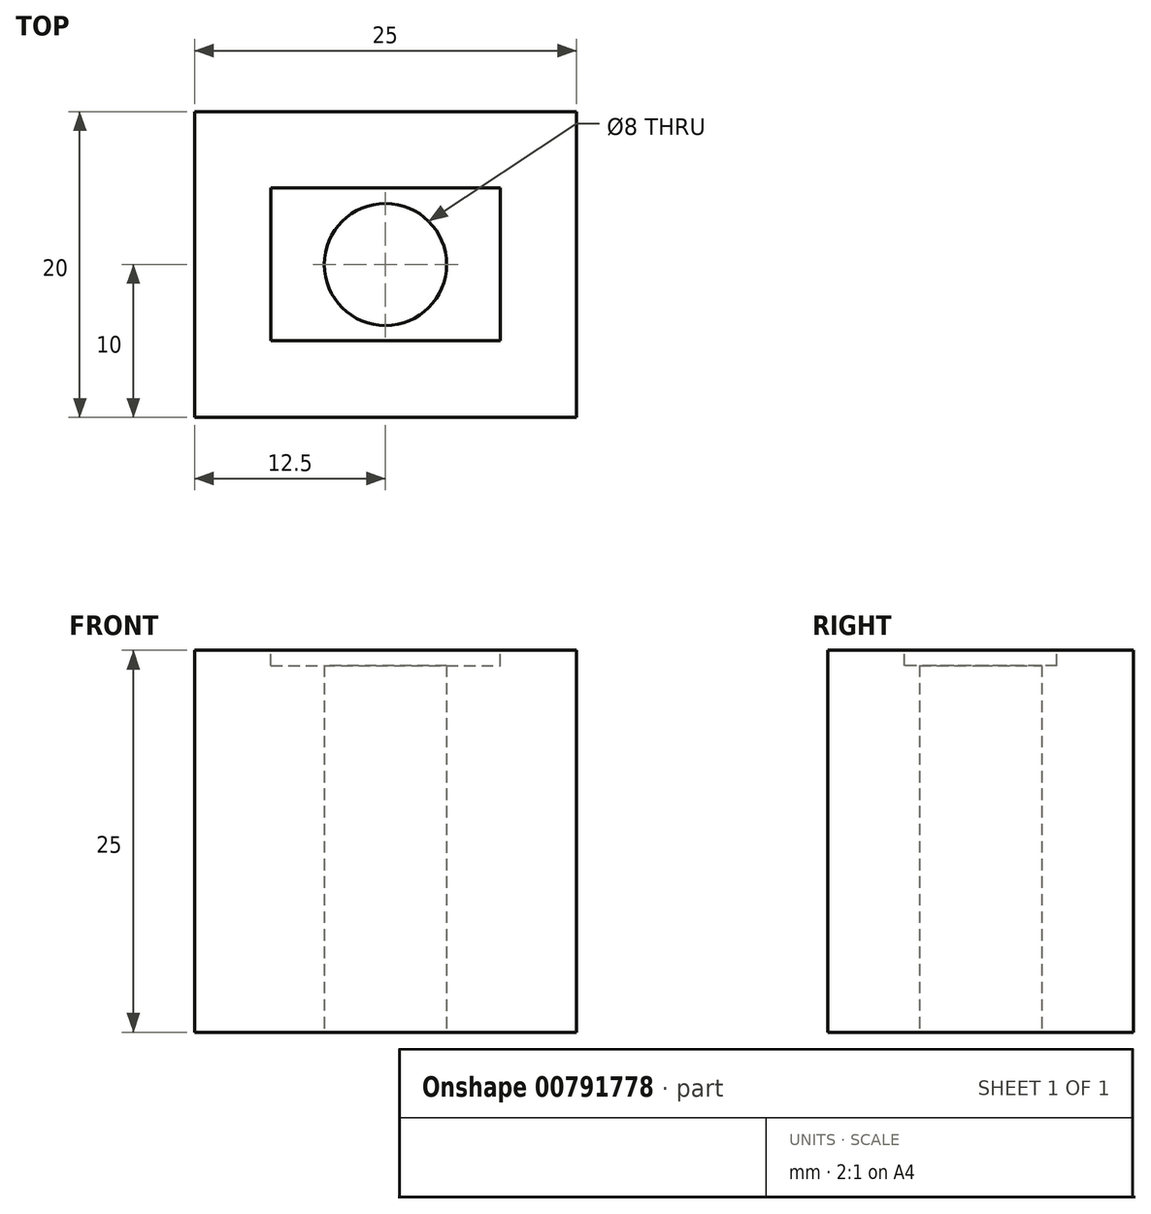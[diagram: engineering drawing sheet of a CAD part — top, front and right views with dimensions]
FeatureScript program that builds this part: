
annotation { "Feature Type Name" : "Feature", "Feature Type Description" : "" }
export const myFeature = defineFeature(function(context is Context, id is Id, definition is map)
    precondition{}
    {
        {
            var Q0;
            Q0=qCreatedBy(makeId("Top.planeOp"),FACE);
            var sketch = newSketch(context, id + "F0", { "sketchPlane" : qUnion([Q0])});
            skLineSegment(sketch, "E0.bottom", {"start": v(-12.5, 10) * mm, "end": v(12.5, 10) * mm});
            skLineSegment(sketch, "E0.top", {"start": v(-12.5, -10) * mm, "end": v(12.5, -10) * mm});
            skLineSegment(sketch, "E0.left", {"start": v(-12.5, 10) * mm, "end": v(-12.5, -10) * mm});
            skLineSegment(sketch, "E0.right", {"start": v(12.5, 10) * mm, "end": v(12.5, -10) * mm});
            skCircle(sketch, "E1", {"center": v(0, 0) * mm, "radius": 4 * mm});
            skSolve(sketch);
        }
        {
            var Q0;
            Q0 = qSketchRegion(id + "F0", true);
            extrude(context, id + "F1", {"entities" : qUnion([Q0]), "depth" : 25 * mm, "offsetDistance" : 25 * mm});
        }
        {
            var Q0;
            Q0=makeQuery(id+"F1.opExtrude","CAP_FACE",FACE,{"disambiguationData":[OSD([sQuery(id+"F0.wireOp",EDGE,"E0.bottom"),sQuery(id+"F0.wireOp",EDGE,"E0.top"),sQuery(id+"F0.wireOp",EDGE,"E0.left"),sQuery(id+"F0.wireOp",EDGE,"E0.right"),sQuery(id+"F0.wireOp",EDGE,"E1")])],"isStart":false});
            var sketch = newSketch(context, id + "F2", { "sketchPlane" : qUnion([Q0])});
            skLineSegment(sketch, "E2.bottom", {"start": v(-7.5, 5) * mm, "end": v(7.5, 5) * mm});
            skLineSegment(sketch, "E2.top", {"start": v(-7.5, -5) * mm, "end": v(7.5, -5) * mm});
            skLineSegment(sketch, "E2.left", {"start": v(-7.5, 5) * mm, "end": v(-7.5, -5) * mm});
            skLineSegment(sketch, "E2.right", {"start": v(7.5, 5) * mm, "end": v(7.5, -5) * mm});
            skSolve(sketch);
        }
        {
            var Q0;
            Q0 = qSketchRegion(id + "F2", true);
            extrude(context, id + "F3", {"entities" : qUnion([Q0]), "operationType" : NewBodyOperationType.REMOVE, "oppositeDirection" : true, "depth" : 1 * mm, "offsetDistance" : 25 * mm});
        }
    });
